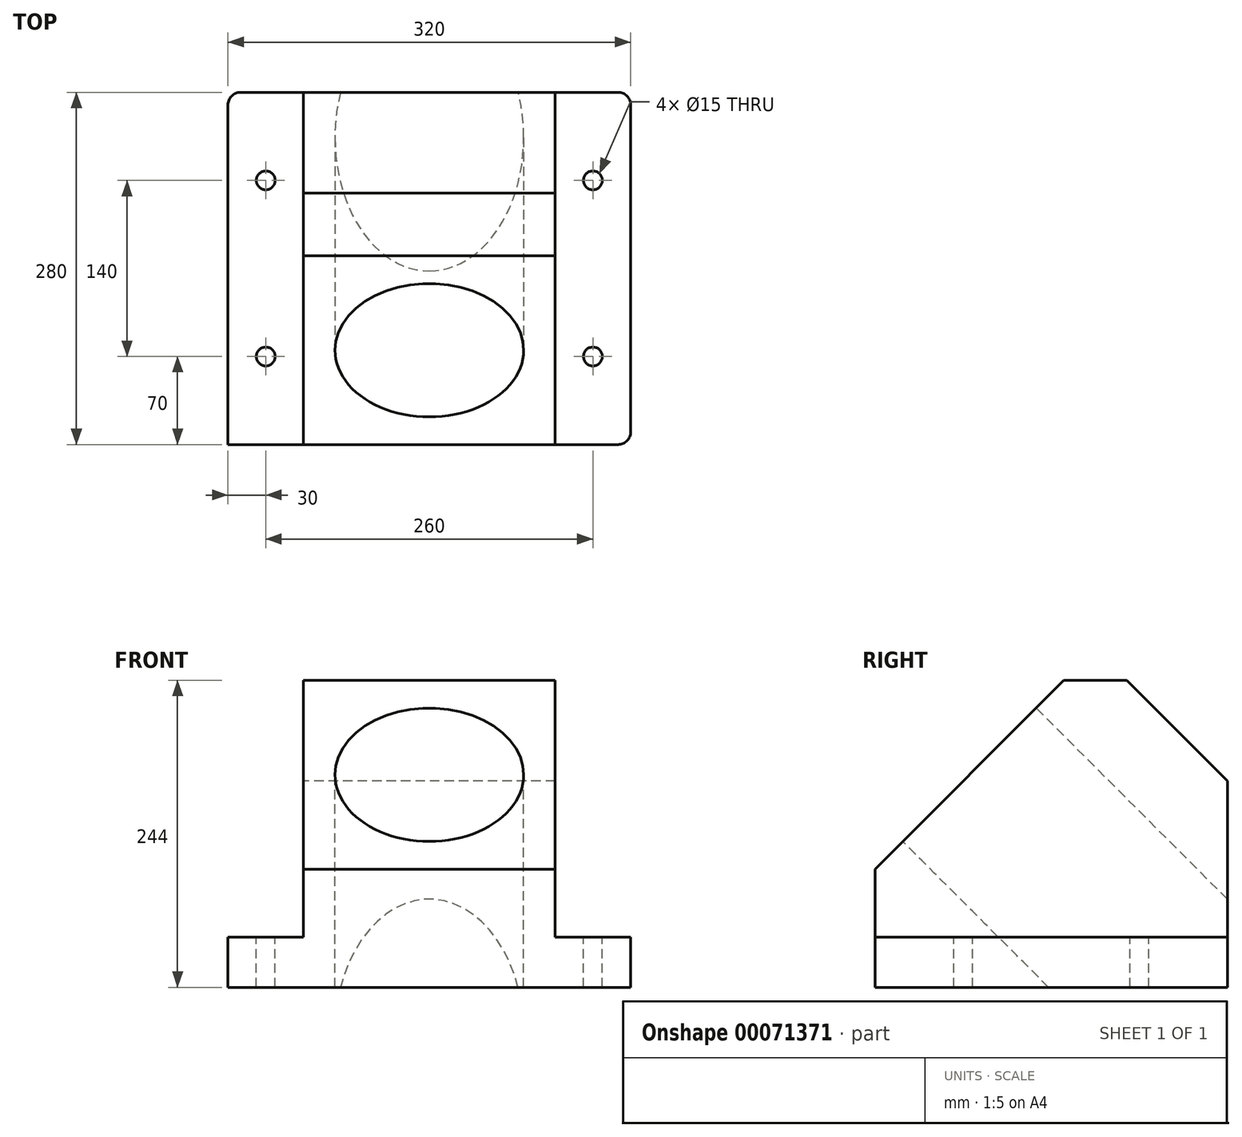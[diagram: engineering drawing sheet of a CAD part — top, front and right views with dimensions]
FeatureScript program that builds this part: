
annotation { "Feature Type Name" : "Feature", "Feature Type Description" : "" }
export const myFeature = defineFeature(function(context is Context, id is Id, definition is map)
    precondition{}
    {
        {
            var Q0;
            Q0=qCreatedBy(makeId("Right.planeOp"),FACE);
            var sketch = newSketch(context, id + "F0", { "sketchPlane" : qUnion([Q0])});
            skLineSegment(sketch, "E0", {"start": v(-150, 0) * mm, "end": v(130, 0) * mm});
            skLineSegment(sketch, "E1", {"start": v(-150, 0) * mm, "end": v(-150, 94) * mm});
            skLineSegment(sketch, "E2", {"start": v(130, 0) * mm, "end": v(130, 164) * mm});
            skLineSegment(sketch, "E3", {"start": v(0, 244) * mm, "end": v(50, 244) * mm});
            skLineSegment(sketch, "E4", {"start": v(-150, 94) * mm, "end": v(0, 244) * mm});
            skLineSegment(sketch, "E5", {"start": v(50, 244) * mm, "end": v(130, 164) * mm});
            skSolve(sketch);
        }
        {
            var Q0;
            Q0=makeQuery(id+"F0.imprint","IMPRINT",FACE,{"disambiguationData":[TD([[makeQuery(id+"F0.imprint","IMPRINT",EDGE,{"derivedFrom":sQuery(id+"F0.wireOp",EDGE,"E0")}),1.0]])]});
            extrude(context, id + "F1", {"entities" : qUnion([Q0]), "depth" : 200 * mm});
        }
        {
            var Q0;
            Q0=makeQuery(id+"F1.opExtrude","CAP_FACE",FACE,{"disambiguationData":[OSD([sQuery(id+"F0.wireOp",EDGE,"E0"),sQuery(id+"F0.wireOp",EDGE,"E1"),sQuery(id+"F0.wireOp",EDGE,"E2"),sQuery(id+"F0.wireOp",EDGE,"E3"),sQuery(id+"F0.wireOp",EDGE,"E4"),sQuery(id+"F0.wireOp",EDGE,"E5")])],"isStart":false});
            var sketch = newSketch(context, id + "F2", { "sketchPlane" : qUnion([Q0])});
            skLineSegment(sketch, "E6", {"start": v(-150, 40) * mm, "end": v(130, 40) * mm});
            skLineSegment(sketch, "E7", {"start": v(130, 40) * mm, "end": v(130, 0) * mm});
            skLineSegment(sketch, "E8", {"start": v(130, 0) * mm, "end": v(-150, 0) * mm});
            skLineSegment(sketch, "E9", {"start": v(-150, 0) * mm, "end": v(-150, 40) * mm});
            skSolve(sketch);
        }
        {
            var Q0;
            Q0=makeQuery(id+"F2.imprint","IMPRINT",FACE,{"disambiguationData":[TD([[makeQuery(id+"F2.imprint","IMPRINT",EDGE,{"derivedFrom":sQuery(id+"F2.wireOp",EDGE,"E6")}),-1.0]])]});
            extrude(context, id + "F3", {"entities" : qUnion([Q0]), "operationType" : NewBodyOperationType.ADD, "depth" : 60 * mm});
        }
        {
            var Q0;
            Q0=makeQuery(id+"F1.opExtrude","CAP_FACE",FACE,{"disambiguationData":[OSD([sQuery(id+"F0.wireOp",EDGE,"E0"),sQuery(id+"F0.wireOp",EDGE,"E1"),sQuery(id+"F0.wireOp",EDGE,"E2"),sQuery(id+"F0.wireOp",EDGE,"E3"),sQuery(id+"F0.wireOp",EDGE,"E4"),sQuery(id+"F0.wireOp",EDGE,"E5")])],"isStart":true});
            var sketch = newSketch(context, id + "F4", { "sketchPlane" : qUnion([Q0])});
            skLineSegment(sketch, "E10", {"start": v(-130, 40) * mm, "end": v(-130, 0) * mm});
            skLineSegment(sketch, "E11", {"start": v(-130, 0) * mm, "end": v(150, 0) * mm});
            skLineSegment(sketch, "E12", {"start": v(-130, 40) * mm, "end": v(150, 40) * mm});
            skLineSegment(sketch, "E13", {"start": v(150, 40) * mm, "end": v(150, 0) * mm});
            skLineSegment(sketch, "E14", {"start": v(150, 0) * mm, "end": v(150, 40) * mm});
            skSolve(sketch);
        }
        {
            var Q0;
            Q0 = qSketchRegion(id + "F4", true);
            extrude(context, id + "F5", {"entities" : qUnion([Q0]), "operationType" : NewBodyOperationType.ADD, "depth" : 60 * mm});
        }
        {
            var Q0;
            Q0=makeQuery(id+"F1.opExtrude","SWEPT_FACE",FACE,{"disambiguationData":[OSD([sQuery(id+"F0.wireOp",EDGE,"E4")])]});
            var sketch = newSketch(context, id + "F6", { "sketchPlane" : qUnion([Q0])});
            skCircle(sketch, "E15", {"center": v(100, 66.47) * mm, "radius": 75 * mm});
            skPoint(sketch, "E15.centerSnap0", {"position": v(0, 66.47) * mm});
            skPoint(sketch, "E15.centerSnap1", {"position": v(100, 172.53) * mm});
            skSolve(sketch);
        }
        {
            var Q0;
            Q0 = qSketchRegion(id + "F6", true);
            extrude(context, id + "F7", {"entities" : qUnion([Q0]), "operationType" : NewBodyOperationType.REMOVE, "oppositeDirection" : true, "depth" : 300 * mm});
        }
        {
            var Q0;
            Q0=makeQuery(id+"F5.opExtrude","SWEPT_FACE",FACE,{"disambiguationData":[OSD([sQuery(id+"F4.wireOp",EDGE,"E12")])]});
            var sketch = newSketch(context, id + "F8", { "sketchPlane" : qUnion([Q0])});
            skLineSegment(sketch, "E16", {"start": v(-60, -10) * mm, "end": v(0, -10) * mm});
            skCircle(sketch, "E17", {"center": v(-30, 60) * mm, "radius": 7.5 * mm});
            skPoint(sketch, "E17.centerSnap0", {"position": v(-30, 130) * mm});
            skCircle(sketch, "E18", {"center": v(-30, -80) * mm, "radius": 7.5 * mm});
            skPoint(sketch, "E18.centerSnap0", {"position": v(-30, -150) * mm});
            skSolve(sketch);
        }
        {
            var Q0;
            Q0=makeQuery(id+"F8.imprint","IMPRINT",FACE,{"disambiguationData":[TD([[makeQuery(id+"F8.imprint","IMPRINT",EDGE,{"derivedFrom":sQuery(id+"F8.wireOp",EDGE,"E17")}),1.0]])]});
            var Q1;
            Q1=makeQuery(id+"F8.imprint","IMPRINT",FACE,{"disambiguationData":[TD([[makeQuery(id+"F8.imprint","IMPRINT",EDGE,{"derivedFrom":sQuery(id+"F8.wireOp",EDGE,"E18")}),1.0]])]});
            extrude(context, id + "F9", {"entities" : qUnion([Q0, Q1]), "operationType" : NewBodyOperationType.REMOVE, "oppositeDirection" : true, "depth" : 40 * mm});
        }
        {
            var Q0;
            Q0=makeQuery(id+"F3.opExtrude","SWEPT_FACE",FACE,{"disambiguationData":[OSD([sQuery(id+"F2.wireOp",EDGE,"E6")])]});
            var sketch = newSketch(context, id + "F10", { "sketchPlane" : qUnion([Q0])});
            skCircle(sketch, "E19", {"center": v(230, 60) * mm, "radius": 7.5 * mm});
            skPoint(sketch, "E19.centerSnap0", {"position": v(230, 130) * mm});
            skCircle(sketch, "E20", {"center": v(230, -80) * mm, "radius": 7.5 * mm});
            skPoint(sketch, "E20.centerSnap0", {"position": v(230, -150) * mm});
            skSolve(sketch);
        }
        {
            var Q0;
            Q0=makeQuery(id+"F10.imprint","IMPRINT",FACE,{"disambiguationData":[TD([[makeQuery(id+"F10.imprint","IMPRINT",EDGE,{"derivedFrom":sQuery(id+"F10.wireOp",EDGE,"E19")}),1.0]])]});
            var Q1;
            Q1=makeQuery(id+"F10.imprint","IMPRINT",FACE,{"disambiguationData":[TD([[makeQuery(id+"F10.imprint","IMPRINT",EDGE,{"derivedFrom":sQuery(id+"F10.wireOp",EDGE,"E20")}),1.0]])]});
            extrude(context, id + "F11", {"entities" : qUnion([Q0, Q1]), "operationType" : NewBodyOperationType.REMOVE, "oppositeDirection" : true, "depth" : 40 * mm});
        }
        {
            var Q0;
            Q0=makeQuery(id+"F5.opExtrude","CAP_EDGE",EDGE,{"disambiguationData":[OSD([sQuery(id+"F4.wireOp",EDGE,"E14")])],"isStart":false});
            var Q1;
            Q1=makeQuery(id+"F3.opExtrude","CAP_EDGE",EDGE,{"disambiguationData":[OSD([sQuery(id+"F2.wireOp",EDGE,"E9")])],"isStart":false});
            var Q2;
            Q2=makeQuery(id+"F3.opExtrude","CAP_EDGE",EDGE,{"disambiguationData":[OSD([sQuery(id+"F2.wireOp",EDGE,"E7")])],"isStart":false});
            var Q3;
            Q3=makeQuery(id+"F5.opExtrude","CAP_EDGE",EDGE,{"disambiguationData":[OSD([sQuery(id+"F4.wireOp",EDGE,"E10")])],"isStart":false});
            fillet(context, id + "F12", {"entities" : qUnion([Q0, Q1, Q2, Q3]), "radius" : 10 * mm, "tangentPropagation" : true, "allowEdgeOverflow" : false});
        }
    });
